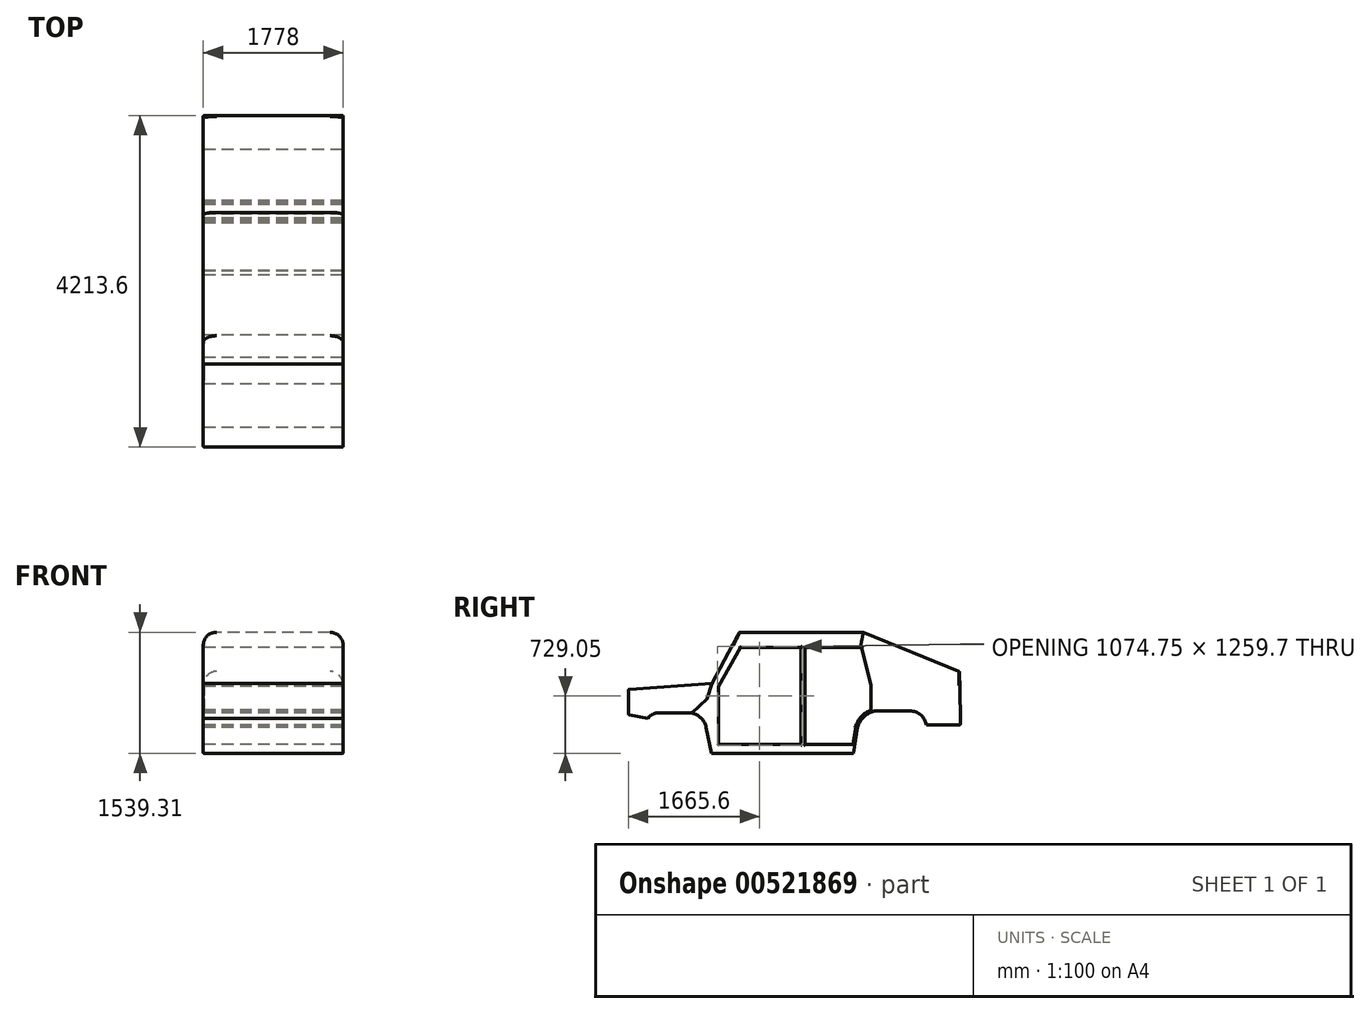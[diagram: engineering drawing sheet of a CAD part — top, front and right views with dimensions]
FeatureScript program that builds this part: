
annotation { "Feature Type Name" : "Feature", "Feature Type Description" : "" }
export const myFeature = defineFeature(function(context is Context, id is Id, definition is map)
    precondition{}
    {
        {
            var Q0;
            Q0=qCreatedBy(makeId("Right.planeOp"),FACE);
            var sketch = newSketch(context, id + "F0", { "sketchPlane" : qUnion([Q0])});
            skLineSegment(sketch, "E0", {"start": v(-1112.1, 194.99) * mm, "end": v(-761.38, 845.18) * mm});
            skLineSegment(sketch, "E1", {"start": v(812.87, 845.25) * mm, "end": v(2035.13, 344.68) * mm});
            skLineSegment(sketch, "E2", {"start": v(1613.65, -334.68) * mm, "end": v(2043.55, -334.68) * mm});
            skLineSegment(sketch, "E3", {"start": v(2035.13, 344.68) * mm, "end": v(2043.55, -334.68) * mm});
            skLineSegment(sketch, "E4", {"start": v(-761.38, 845.18) * mm, "end": v(812.87, 845.25) * mm});
            skLineSegment(sketch, "E5", {"start": v(-2170.2, 120.63) * mm, "end": v(-1112.1, 194.99) * mm});
            skLineSegment(sketch, "E6", {"start": v(-2170.2, 120.63) * mm, "end": v(-2170.2, -203.25) * mm});
            skPoint(sketch, "E6.endSnap0", {"position": v(-2169.6, -203.25) * mm});
            skArc(sketch, "E7", {"start": v(-1182.84, -365.23) * mm, "mid": v(-1246.86, -246.08) * mm, "end": v(-1365.3, -180.74) * mm});
            skLineSegment(sketch, "E8", {"start": v(-1365.3, -180.74) * mm, "end": v(-1795.76, -180.74) * mm});
            skArc(sketch, "E9", {"start": v(-1795.76, -180.74) * mm, "mid": v(-1866.93, -198.92) * mm, "end": v(-1920.67, -249) * mm});
            skLineSegment(sketch, "E10", {"start": v(-2170.2, -203.25) * mm, "end": v(-1920.67, -249) * mm});
            skLineSegment(sketch, "E11", {"start": v(966.35, -155.13) * mm, "end": v(1404.71, -155.8) * mm});
            skPoint(sketch, "E11.endSnap0", {"position": v(1148.73, -155.8) * mm});
            skArc(sketch, "E12", {"start": v(1404.71, -155.8) * mm, "mid": v(1542.16, -206.72) * mm, "end": v(1613.65, -334.68) * mm});
            skLineSegment(sketch, "E13", {"start": v(811.6, 677.54) * mm, "end": v(937.55, 176.02) * mm});
            skLineSegment(sketch, "E14", {"start": v(2006.61, 176.02) * mm, "end": v(937.55, 176.02) * mm});
            skLineSegment(sketch, "E15", {"start": v(2006.61, 176.02) * mm, "end": v(2037.22, 176.02) * mm});
            skLineSegment(sketch, "E16", {"start": v(-1114.66, -694.06) * mm, "end": v(687.1, -694.06) * mm});
            skLineSegment(sketch, "E17", {"start": v(-1182.84, -365.23) * mm, "end": v(-1114.66, -694.06) * mm});
            skLineSegment(sketch, "E18", {"start": v(937.55, 176.02) * mm, "end": v(937.55, -162.04) * mm});
            skCircle(sketch, "E19", {"center": v(-1592.83, -615.33) * mm, "radius": 344.3 * mm});
            skCircle(sketch, "E20", {"center": v(1124.97, -614.06) * mm, "radius": 344.3 * mm});
            skLineSegment(sketch, "E21", {"start": v(-1054.68, -607.56) * mm, "end": v(45.47, -607.56) * mm});
            skLineSegment(sketch, "E22", {"start": v(45.47, -607.56) * mm, "end": v(701.12, -607.56) * mm});
            skLineSegment(sketch, "E23", {"start": v(-1054.68, -607.56) * mm, "end": v(-1054.68, 160.79) * mm});
            skLineSegment(sketch, "E24", {"start": v(-1054.68, 160.79) * mm, "end": v(-761.92, 677.54) * mm});
            skLineSegment(sketch, "E25", {"start": v(45.47, -607.56) * mm, "end": v(45.47, 677.54) * mm});
            skLineSegment(sketch, "E26", {"start": v(-761.92, 677.54) * mm, "end": v(45.47, 677.54) * mm});
            skLineSegment(sketch, "E27", {"start": v(45.47, 677.54) * mm, "end": v(811.6, 677.54) * mm});
            skLineSegment(sketch, "E28", {"start": v(45.47, 677.54) * mm, "end": v(45.47, -607.56) * mm});
            skLineSegment(sketch, "E29.0", {"start": v(20.07, 652.14) * mm, "end": v(20.07, -582.16) * mm});
            skLineSegment(sketch, "E29.1", {"start": v(-747.12, 652.14) * mm, "end": v(20.07, 652.14) * mm});
            skLineSegment(sketch, "E29.2", {"start": v(-1029.28, -582.16) * mm, "end": v(20.07, -582.16) * mm});
            skLineSegment(sketch, "E29.3", {"start": v(-1029.28, -582.16) * mm, "end": v(-1029.28, 154.1) * mm});
            skLineSegment(sketch, "E29.4", {"start": v(-1029.28, 154.1) * mm, "end": v(-747.12, 652.14) * mm});
            skArc(sketch, "E30", {"start": v(937.55, -162.04) * mm, "mid": v(812.92, -236.19) * mm, "end": v(740.9, -362.07) * mm});
            skArc(sketch, "E31", {"start": v(966.35, -155.13) * mm, "mid": v(951.65, -157.32) * mm, "end": v(937.55, -162.04) * mm});
            skLineSegment(sketch, "E32", {"start": v(701.12, -607.56) * mm, "end": v(740.9, -362.07) * mm});
            skLineSegment(sketch, "E33", {"start": v(687.1, -694.06) * mm, "end": v(701.12, -607.56) * mm});
            skLineSegment(sketch, "E34.0", {"start": v(70.87, -582.16) * mm, "end": v(679.5, -582.16) * mm});
            skLineSegment(sketch, "E34.1", {"start": v(679.5, -582.16) * mm, "end": v(716.04, -356.75) * mm});
            skLineSegment(sketch, "E34.2", {"start": v(70.87, 652.14) * mm, "end": v(791.8, 652.14) * mm});
            skLineSegment(sketch, "E34.3", {"start": v(791.8, 652.14) * mm, "end": v(912.15, 172.88) * mm});
            skLineSegment(sketch, "E34.4", {"start": v(912.15, 172.88) * mm, "end": v(912.15, -143.53) * mm});
            skLineSegment(sketch, "E34.5", {"start": v(70.87, -582.16) * mm, "end": v(70.87, 652.14) * mm});
            skArc(sketch, "E34.6", {"start": v(912.15, -143.53) * mm, "mid": v(787.7, -225.86) * mm, "end": v(716.04, -356.75) * mm});
            skLineSegment(sketch, "E35", {"start": v(-1112.1, 194.99) * mm, "end": v(-1172.06, 0) * mm});
            skLineSegment(sketch, "E36", {"start": v(-1172.06, 0) * mm, "end": v(-1365.3, -180.74) * mm});
            skSolve(sketch);
        }
        {
            var Q0;
            Q0=makeQuery(id+"F0.imprint","IMPRINT",FACE,{"disambiguationData":[TD([[makeQuery(id+"F0.imprint","IMPRINT",EDGE,{"derivedFrom":sQuery(id+"F0.wireOp",EDGE,"E29.0")}),-1.0]])]});
            extrude(context, id + "F1", {"entities" : qUnion([Q0]), "endBound" : BoundingType.SYMMETRIC, "depth" : 1778 * mm, "offsetDistance" : 25.4 * mm});
        }
        {
            var Q0;
            Q0=makeQuery(id+"F0.imprint","IMPRINT",FACE,{"disambiguationData":[TD([[makeQuery(id+"F0.imprint","IMPRINT",EDGE,{"derivedFrom":sQuery(id+"F0.wireOp",EDGE,"E34.0")}),1.0]])]});
            extrude(context, id + "F2", {"entities" : qUnion([Q0]), "endBound" : BoundingType.SYMMETRIC, "depth" : 1778 * mm, "offsetDistance" : 25.4 * mm});
        }
        {
            var Q0;
            Q0=makeQuery(id+"F1.opExtrude","CAP_FACE",FACE,{"disambiguationData":[OSD([sQuery(id+"F0.wireOp",EDGE,"E29.0"),sQuery(id+"F0.wireOp",EDGE,"E29.1"),sQuery(id+"F0.wireOp",EDGE,"E29.2"),sQuery(id+"F0.wireOp",EDGE,"E29.3"),sQuery(id+"F0.wireOp",EDGE,"E29.4")])],"isStart":false});
            var Q1;
            Q1=makeQuery(id+"F2.opExtrude","CAP_FACE",FACE,{"disambiguationData":[OSD([sQuery(id+"F0.wireOp",EDGE,"E34.0"),sQuery(id+"F0.wireOp",EDGE,"E34.1"),sQuery(id+"F0.wireOp",EDGE,"E34.2"),sQuery(id+"F0.wireOp",EDGE,"E34.3"),sQuery(id+"F0.wireOp",EDGE,"E34.4"),sQuery(id+"F0.wireOp",EDGE,"E34.5"),sQuery(id+"F0.wireOp",EDGE,"E34.6")])],"isStart":false});
            var Q2;
            Q2=makeQuery(id+"F2.opExtrude","CAP_FACE",FACE,{"disambiguationData":[OSD([sQuery(id+"F0.wireOp",EDGE,"E34.0"),sQuery(id+"F0.wireOp",EDGE,"E34.1"),sQuery(id+"F0.wireOp",EDGE,"E34.2"),sQuery(id+"F0.wireOp",EDGE,"E34.3"),sQuery(id+"F0.wireOp",EDGE,"E34.4"),sQuery(id+"F0.wireOp",EDGE,"E34.5"),sQuery(id+"F0.wireOp",EDGE,"E34.6")])],"isStart":true});
            var Q3;
            Q3=makeQuery(id+"F1.opExtrude","CAP_FACE",FACE,{"disambiguationData":[OSD([sQuery(id+"F0.wireOp",EDGE,"E29.0"),sQuery(id+"F0.wireOp",EDGE,"E29.1"),sQuery(id+"F0.wireOp",EDGE,"E29.2"),sQuery(id+"F0.wireOp",EDGE,"E29.3"),sQuery(id+"F0.wireOp",EDGE,"E29.4")])],"isStart":true});
            fillet(context, id + "F3", {"entities" : qUnion([Q0, Q1, Q2, Q3]), "radius" : 12.7 * mm, "tangentPropagation" : true, "allowEdgeOverflow" : false});
        }
        {
            var Q0;
            Q0=makeQuery(id+"F0.imprint","IMPRINT",FACE,{"disambiguationData":[TD([[makeQuery(id+"F0.imprint","IMPRINT",EDGE,{"derivedFrom":sQuery(id+"F0.wireOp",EDGE,"E0")}),-1.0]])]});
            var Q1;
            {var subQ0=sQuery(id+"F0.wireOp",EDGE,"E2");Q1=makeQuery(id+"F0.imprint","IMPRINT",FACE,{"disambiguationData":[TD([[makeQuery(id+"F0.imprint","IMPRINT",EDGE,{"derivedFrom":subQ0}),1.0]])]});}
            var Q2;
            Q2=makeQuery(id+"F0.imprint","IMPRINT",FACE,{"disambiguationData":[TD([[makeQuery(id+"F0.imprint","IMPRINT",EDGE,{"derivedFrom":sQuery(id+"F0.wireOp",EDGE,"E13")}),-1.0]])]});
            var Q3;
            Q3=makeQuery(id+"F0.imprint","IMPRINT",FACE,{"disambiguationData":[TD([[makeQuery(id+"F0.imprint","IMPRINT",EDGE,{"derivedFrom":sQuery(id+"F0.wireOp",EDGE,"E21")}),1.0]])]});
            extrude(context, id + "F4", {"entities" : qUnion([Q0, Q1, Q2, Q3]), "endBound" : BoundingType.SYMMETRIC, "depth" : 1778 * mm, "offsetDistance" : 25.4 * mm});
        }
        {
            var Q0;
            Q0=makeQuery(id+"F4.opExtrude","CAP_EDGE",EDGE,{"disambiguationData":[OSD([sQuery(id+"F0.wireOp",EDGE,"E4")])],"isStart":false});
            var Q1;
            Q1=makeQuery(id+"F4.opExtrude","CAP_EDGE",EDGE,{"disambiguationData":[OSD([sQuery(id+"F0.wireOp",EDGE,"E1")])],"isStart":false});
            var Q2;
            Q2=makeQuery(id+"F4.opExtrude","CAP_EDGE",EDGE,{"disambiguationData":[OSD([sQuery(id+"F0.wireOp",EDGE,"E1")])],"isStart":true});
            var Q3;
            Q3=makeQuery(id+"F4.opExtrude","CAP_EDGE",EDGE,{"disambiguationData":[OSD([sQuery(id+"F0.wireOp",EDGE,"E4")])],"isStart":true});
            fillet(context, id + "F5", {"entities" : qUnion([Q0, Q1, Q2, Q3]), "radius" : 167.64 * mm, "tangentPropagation" : true, "allowEdgeOverflow" : false});
        }
        {
            var Q0;
            Q0=makeQuery(id+"F4.opExtrude","CAP_FACE",FACE,{"disambiguationData":[OSD([sQuery(id+"F0.wireOp",EDGE,"E0"),sQuery(id+"F0.wireOp",EDGE,"E1"),sQuery(id+"F0.wireOp",EDGE,"E2"),sQuery(id+"F0.wireOp",EDGE,"E3"),sQuery(id+"F0.wireOp",EDGE,"E4"),sQuery(id+"F0.wireOp",EDGE,"E7"),sQuery(id+"F0.wireOp",EDGE,"E11"),sQuery(id+"F0.wireOp",EDGE,"E12"),sQuery(id+"F0.wireOp",EDGE,"E16"),sQuery(id+"F0.wireOp",EDGE,"E17"),sQuery(id+"F0.wireOp",EDGE,"E29.0"),sQuery(id+"F0.wireOp",EDGE,"E29.1"),sQuery(id+"F0.wireOp",EDGE,"E29.2"),sQuery(id+"F0.wireOp",EDGE,"E29.3"),sQuery(id+"F0.wireOp",EDGE,"E29.4"),sQuery(id+"F0.wireOp",EDGE,"E30"),sQuery(id+"F0.wireOp",EDGE,"E31"),sQuery(id+"F0.wireOp",EDGE,"E32"),sQuery(id+"F0.wireOp",EDGE,"E33"),sQuery(id+"F0.wireOp",EDGE,"E34.0"),sQuery(id+"F0.wireOp",EDGE,"E34.1"),sQuery(id+"F0.wireOp",EDGE,"E34.2"),sQuery(id+"F0.wireOp",EDGE,"E34.3"),sQuery(id+"F0.wireOp",EDGE,"E34.4"),sQuery(id+"F0.wireOp",EDGE,"E34.5"),sQuery(id+"F0.wireOp",EDGE,"E34.6"),sQuery(id+"F0.wireOp",EDGE,"E35"),sQuery(id+"F0.wireOp",EDGE,"E36")])],"isStart":false});
            var Q1;
            Q1=makeQuery(id+"F4.opExtrude","CAP_FACE",FACE,{"disambiguationData":[OSD([sQuery(id+"F0.wireOp",EDGE,"E0"),sQuery(id+"F0.wireOp",EDGE,"E1"),sQuery(id+"F0.wireOp",EDGE,"E2"),sQuery(id+"F0.wireOp",EDGE,"E3"),sQuery(id+"F0.wireOp",EDGE,"E4"),sQuery(id+"F0.wireOp",EDGE,"E7"),sQuery(id+"F0.wireOp",EDGE,"E11"),sQuery(id+"F0.wireOp",EDGE,"E12"),sQuery(id+"F0.wireOp",EDGE,"E16"),sQuery(id+"F0.wireOp",EDGE,"E17"),sQuery(id+"F0.wireOp",EDGE,"E29.0"),sQuery(id+"F0.wireOp",EDGE,"E29.1"),sQuery(id+"F0.wireOp",EDGE,"E29.2"),sQuery(id+"F0.wireOp",EDGE,"E29.3"),sQuery(id+"F0.wireOp",EDGE,"E29.4"),sQuery(id+"F0.wireOp",EDGE,"E30"),sQuery(id+"F0.wireOp",EDGE,"E31"),sQuery(id+"F0.wireOp",EDGE,"E32"),sQuery(id+"F0.wireOp",EDGE,"E33"),sQuery(id+"F0.wireOp",EDGE,"E34.0"),sQuery(id+"F0.wireOp",EDGE,"E34.1"),sQuery(id+"F0.wireOp",EDGE,"E34.2"),sQuery(id+"F0.wireOp",EDGE,"E34.3"),sQuery(id+"F0.wireOp",EDGE,"E34.4"),sQuery(id+"F0.wireOp",EDGE,"E34.5"),sQuery(id+"F0.wireOp",EDGE,"E34.6"),sQuery(id+"F0.wireOp",EDGE,"E35"),sQuery(id+"F0.wireOp",EDGE,"E36")])],"isStart":true});
            fillet(context, id + "F6", {"entities" : qUnion([Q0, Q1]), "radius" : 12.7 * mm, "tangentPropagation" : true, "allowEdgeOverflow" : false});
        }
        {
            var Q0;
            Q0=makeQuery(id+"F0.imprint","IMPRINT",FACE,{"disambiguationData":[TD([[makeQuery(id+"F0.imprint","IMPRINT",EDGE,{"derivedFrom":sQuery(id+"F0.wireOp",EDGE,"E5")}),-1.0]])]});
            extrude(context, id + "F7", {"entities" : qUnion([Q0]), "operationType" : NewBodyOperationType.ADD, "endBound" : BoundingType.SYMMETRIC, "depth" : 1778 * mm, "offsetDistance" : 25.4 * mm});
        }
        {
            var Q0;
            Q0=makeQuery(id+"F7.opExtrude","CAP_FACE",FACE,{"disambiguationData":[OSD([sQuery(id+"F0.wireOp",EDGE,"E5"),sQuery(id+"F0.wireOp",EDGE,"E6"),sQuery(id+"F0.wireOp",EDGE,"E8"),sQuery(id+"F0.wireOp",EDGE,"E9"),sQuery(id+"F0.wireOp",EDGE,"E10"),sQuery(id+"F0.wireOp",EDGE,"E35"),sQuery(id+"F0.wireOp",EDGE,"E36")])],"isStart":false});
            var Q1;
            Q1=makeQuery(id+"F7.opExtrude","SWEPT_FACE",FACE,{"disambiguationData":[OSD([sQuery(id+"F0.wireOp",EDGE,"E6")])]});
            var Q2;
            Q2=makeQuery(id+"F7.opExtrude","CAP_FACE",FACE,{"disambiguationData":[OSD([sQuery(id+"F0.wireOp",EDGE,"E5"),sQuery(id+"F0.wireOp",EDGE,"E6"),sQuery(id+"F0.wireOp",EDGE,"E8"),sQuery(id+"F0.wireOp",EDGE,"E9"),sQuery(id+"F0.wireOp",EDGE,"E10"),sQuery(id+"F0.wireOp",EDGE,"E35"),sQuery(id+"F0.wireOp",EDGE,"E36")])],"isStart":true});
            fillet(context, id + "F8", {"entities" : qUnion([Q0, Q1, Q2]), "radius" : 12.7 * mm, "tangentPropagation" : true, "allowEdgeOverflow" : false});
        }
        {
            var Q0;
            Q0=makeQuery(id+"F4.opExtrude","SWEPT_EDGE",EDGE,{"disambiguationData":[OSD([sQuery(id+"F0.wireOp",EDGE,"E2"),sQuery(id+"F0.wireOp",EDGE,"E3")])]});
            fillet(context, id + "F9", {"entities" : qUnion([Q0]), "radius" : 12.7 * mm, "tangentPropagation" : true, "allowEdgeOverflow" : false});
        }
        {
            var Q0;
            Q0=makeQuery(id+"F1.opExtrude","CAP_FACE",FACE,{"disambiguationData":[OSD([sQuery(id+"F0.wireOp",EDGE,"E29.0"),sQuery(id+"F0.wireOp",EDGE,"E29.1"),sQuery(id+"F0.wireOp",EDGE,"E29.2"),sQuery(id+"F0.wireOp",EDGE,"E29.3"),sQuery(id+"F0.wireOp",EDGE,"E29.4")])],"isStart":false});
            var Q1;
            Q1=makeQuery(id+"F1.opExtrude","SWEPT_BODY",BODY,{"disambiguationData":[OSD([sQuery(id+"F0.wireOp",EDGE,"E29.0"),sQuery(id+"F0.wireOp",EDGE,"E29.1"),sQuery(id+"F0.wireOp",EDGE,"E29.2"),sQuery(id+"F0.wireOp",EDGE,"E29.3"),sQuery(id+"F0.wireOp",EDGE,"E29.4")])]});
            shell(context, id + "F10", {"isHollow" : true, "entities" : qUnion([Q0]), "parts" : qUnion([Q1]), "thickness" : 1.59 * mm});
        }
        {
            var Q0;
            Q0=makeQuery(id+"F2.opExtrude","CAP_FACE",FACE,{"disambiguationData":[OSD([sQuery(id+"F0.wireOp",EDGE,"E34.0"),sQuery(id+"F0.wireOp",EDGE,"E34.1"),sQuery(id+"F0.wireOp",EDGE,"E34.2"),sQuery(id+"F0.wireOp",EDGE,"E34.3"),sQuery(id+"F0.wireOp",EDGE,"E34.4"),sQuery(id+"F0.wireOp",EDGE,"E34.5"),sQuery(id+"F0.wireOp",EDGE,"E34.6")])],"isStart":false});
            var Q1;
            Q1=makeQuery(id+"F2.opExtrude","SWEPT_BODY",BODY,{"disambiguationData":[OSD([sQuery(id+"F0.wireOp",EDGE,"E34.0"),sQuery(id+"F0.wireOp",EDGE,"E34.1"),sQuery(id+"F0.wireOp",EDGE,"E34.2"),sQuery(id+"F0.wireOp",EDGE,"E34.3"),sQuery(id+"F0.wireOp",EDGE,"E34.4"),sQuery(id+"F0.wireOp",EDGE,"E34.5"),sQuery(id+"F0.wireOp",EDGE,"E34.6")])]});
            shell(context, id + "F11", {"isHollow" : true, "entities" : qUnion([Q0]), "parts" : qUnion([Q1]), "thickness" : 1.59 * mm});
        }
        {
            var Q0;
            Q0=makeQuery(id+"F1.opExtrude","SWEPT_BODY",BODY,{"disambiguationData":[OSD([sQuery(id+"F0.wireOp",EDGE,"E29.0"),sQuery(id+"F0.wireOp",EDGE,"E29.1"),sQuery(id+"F0.wireOp",EDGE,"E29.2"),sQuery(id+"F0.wireOp",EDGE,"E29.3"),sQuery(id+"F0.wireOp",EDGE,"E29.4")])]});
            transform(context, id + "F12", {"entities" : qUnion([Q0]), "transformType" : TransformType.TRANSLATION_3D, "dx" : 0 * mm, "dy" : 0 * mm, "dz" : 0 * mm, "makeCopy" : true});
        }
    });
